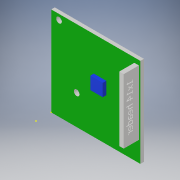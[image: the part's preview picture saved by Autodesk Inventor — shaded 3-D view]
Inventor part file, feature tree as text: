
AUTODESK INVENTOR PART (.ipt)
format: ipt  version: 2017 (Build 210142000, 142)  size: 384,512 bytes
history: native  units: in
note: dims shown in document units (in); Inventor stores cm internally (conversion verified against a paired STEP export)
features: sketch x6, extrude x4
ambient origin geometry x8: Origin, YZ Plane, XZ Plane, XY Plane, X Axis, Y Axis, Z Axis, Center Point
bodies: Solid3 (feature_tree), Solid4 (feature_tree)
feature tree (10):
  sketch  "Sketch1"  dims[d0=1.9685in d1=1.9685in]
  sketch  "Sketch2"  dims[d2=0.126in d3=0.126in]
  sketch  "Sketch7"  dims[d23=0.126in d28=0.2756in]
  extrude  "Extrusion4"  Depth=1.9685in
  extrude  "Extrusion5"  Depth=0.126in
  extrude  "Extrusion6"  Depth=0.2756in
  sketch  "Sketch9"  dims[d31=90.0deg]
  extrude  "Extrusion7"  Depth=0.2756in
  sketch  "Sketch8"  dims[d29=0.2756in d30=0.2756in]
  sketch  "Sketch14"  dims[d32=0.2756in d33=0.2756in d34=0.2756in d35=90.0deg d36=0.0787in d37=0.0in d38=0.0787in d39=0.0in d47=0.3346in d48=0.0in d49=0.3937in d50=0.0in]
